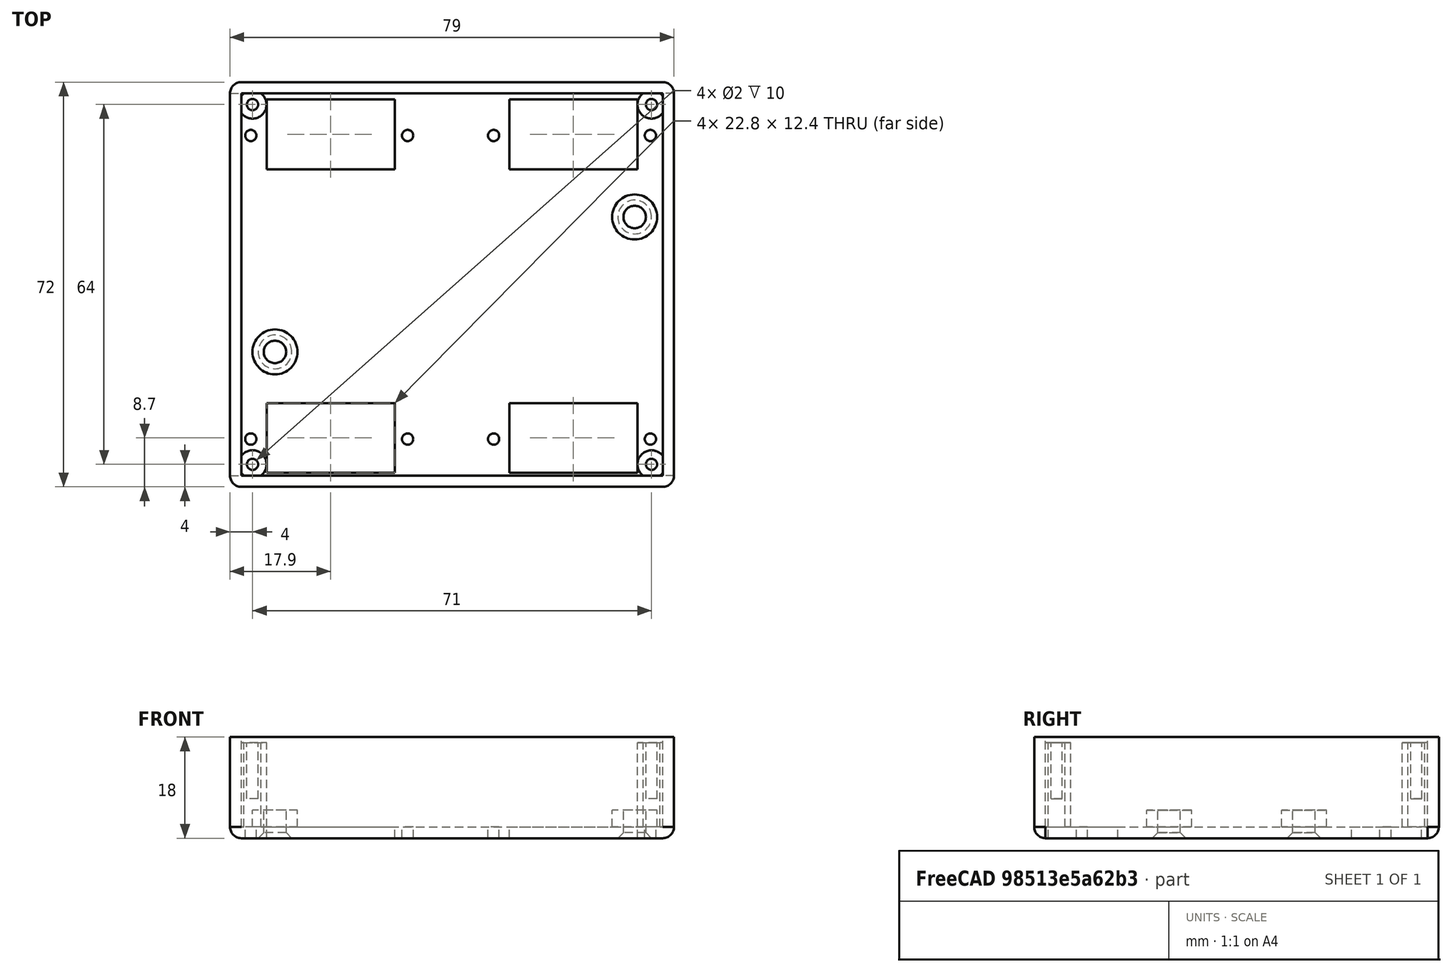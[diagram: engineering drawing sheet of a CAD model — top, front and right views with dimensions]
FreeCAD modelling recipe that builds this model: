
FCSTD DOCUMENT  (FreeCAD 0.18R16131 (Git))
Label: Level crossing base5 n gauge
License: All rights reserved
LicenseURL: http://en.wikipedia.org/wiki/All_rights_reserved
objects: PartDesign::LinearPattern×9, PartDesign::MultiTransform×4, PartDesign::SubtractiveCylinder×4, PartDesign::AdditiveCylinder×3, PartDesign::Chamfer×2, PartDesign::AdditiveBox×1, PartDesign::Thickness×1, PartDesign::SubtractiveBox×1, PartDesign::Body×1
note: 35 computed .brp shape members not serialized (recipe doc carries the construction recipe); baked Part::Feature solids carry a one-line shape summary decoded from their .brp

FEATURE [PartDesign::AdditiveBox] Box
  AttacherType = Attacher::AttachEngine3D
  Height = 16
  Length = 75
  MapMode = 5
  Support = -> [XY_Plane]
  Width = 67.45
FEATURE [PartDesign::Thickness] Thickness
  Base = -> Box [Face6]
  BaseFeature = -> Box
  Join = 0
  Mode = 0
  Value = 2
FEATURE [PartDesign::SubtractiveBox] Box001
  AttacherType = Attacher::AttachEngine3D
  AttachmentOffset = pos=(4.5,0.5,-2) rot=(0,0,1;0rad)
  BaseFeature = -> Thickness
  Height = 2
  Length = 22.8
  MapMode = 5
  Placement = pos=(4.5,0.5,-2) rot=(0,0,1;0rad)
  Support = -> [XY_Plane]
  Width = 12.4
FEATURE [PartDesign::LinearPattern] LinearPattern
  Direction = -> X_Axis
  Length = 43.2
  Occurrences = 2
  Placement = pos=(4.5,0.5,-2) rot=(0,0,1;0rad)
FEATURE [PartDesign::LinearPattern] LinearPattern001
  Direction = -> Y_Axis
  Length = 54
  Occurrences = 2
  Placement = pos=(4.5,0.5,-2) rot=(0,0,1;0rad)
FEATURE [PartDesign::MultiTransform] MultiTransform
  BaseFeature = -> Box001
  Originals = -> [Box001]
  Placement = pos=(4.5,0.5,-2) rot=(0,0,1;0rad)
  Transformations = -> [LinearPattern,LinearPattern001]
FEATURE [PartDesign::SubtractiveCylinder] Cylinder
  Angle = 360
  AttacherType = Attacher::AttachEngine3D
  AttachmentOffset = pos=(1.7,6.5,-2) rot=(0,0,1;0rad)
  BaseFeature = -> MultiTransform
  Height = 2
  MapMode = 5
  Placement = pos=(1.7,6.5,-2) rot=(0,0,1;0rad)
  Radius = 1
  Support = -> [XY_Plane]
FEATURE [PartDesign::LinearPattern] LinearPattern002
  Direction = -> X_Axis
  Length = 43.2
  Occurrences = 2
  Placement = pos=(1.7,6.5,-2) rot=(0,0,1;0rad)
FEATURE [PartDesign::LinearPattern] LinearPattern003
  Direction = -> Y_Axis
  Length = 54
  Occurrences = 2
  Placement = pos=(1.7,6.5,-2) rot=(0,0,1;0rad)
FEATURE [PartDesign::LinearPattern] LinearPattern004
  Direction = -> X_Axis
  Length = 27.9
  Occurrences = 2
  Placement = pos=(1.7,6.5,-2) rot=(0,0,1;0rad)
FEATURE [PartDesign::MultiTransform] MultiTransform001
  BaseFeature = -> Cylinder
  Originals = -> [Cylinder]
  Placement = pos=(1.7,6.5,-2) rot=(0,0,1;0rad)
  Transformations = -> [LinearPattern002,LinearPattern003,LinearPattern004]
FEATURE [PartDesign::AdditiveCylinder] Cylinder001
  Angle = 360
  AttacherType = Attacher::AttachEngine3D
  AttachmentOffset = pos=(2,2,0) rot=(0,0,1;0rad)
  BaseFeature = -> MultiTransform001
  Height = 15
  MapMode = 5
  Placement = pos=(2,2,0) rot=(0,0,1;0rad)
  Radius = 2.5
  Support = -> [XY_Plane]
FEATURE [PartDesign::LinearPattern] LinearPattern005
  Direction = -> X_Axis
  Length = 71
  Occurrences = 2
  Placement = pos=(2,2,0) rot=(0,0,1;0rad)
FEATURE [PartDesign::LinearPattern] LinearPattern006
  Direction = -> Y_Axis
  Length = 64
  Occurrences = 2
  Placement = pos=(2,2,0) rot=(0,0,1;0rad)
FEATURE [PartDesign::MultiTransform] MultiTransform002
  BaseFeature = -> Cylinder001
  Originals = -> [Cylinder001]
  Placement = pos=(2,2,0) rot=(0,0,1;0rad)
  Transformations = -> [LinearPattern005,LinearPattern006]
FEATURE [PartDesign::SubtractiveCylinder] Cylinder002
  Angle = 360
  AttacherType = Attacher::AttachEngine3D
  AttachmentOffset = pos=(0,0,-10) rot=(0,0,1;0rad)
  BaseFeature = -> MultiTransform002
  Height = 10
  MapMode = 5
  Placement = pos=(2,2,5) rot=(0,0,1;0rad)
  Radius = 1
  Support = -> [MultiTransform002]
FEATURE [PartDesign::LinearPattern] LinearPattern007
  Direction = -> X_Axis
  Length = 71
  Occurrences = 2
  Placement = pos=(2,2,5) rot=(0,0,1;0rad)
FEATURE [PartDesign::LinearPattern] LinearPattern008
  Direction = -> Y_Axis
  Length = 64
  Occurrences = 2
  Placement = pos=(2,2,5) rot=(0,0,1;0rad)
FEATURE [PartDesign::MultiTransform] MultiTransform003
  BaseFeature = -> Cylinder002
  Originals = -> [Cylinder002]
  Placement = pos=(2,2,5) rot=(0,0,1;0rad)
  Transformations = -> [LinearPattern007,LinearPattern008]
FEATURE [PartDesign::AdditiveCylinder] Cylinder003
  Angle = 360
  AttacherType = Attacher::AttachEngine3D
  AttachmentOffset = pos=(6,22,0) rot=(0,0,1;0rad)
  BaseFeature = -> MultiTransform003
  Height = 3
  MapMode = 5
  Placement = pos=(6,22,0) rot=(0,0,1;0rad)
  Radius = 4
  Support = -> [XY_Plane]
FEATURE [PartDesign::AdditiveCylinder] Cylinder004
  Angle = 360
  AttacherType = Attacher::AttachEngine3D
  AttachmentOffset = pos=(70,46,0) rot=(0,0,1;0rad)
  BaseFeature = -> Cylinder003
  Height = 3
  MapMode = 5
  Placement = pos=(70,46,0) rot=(0,0,1;0rad)
  Radius = 4
  Support = -> [XY_Plane]
FEATURE [PartDesign::SubtractiveCylinder] Cylinder005
  Angle = 360
  AttacherType = Attacher::AttachEngine3D
  AttachmentOffset = pos=(6,22,-2) rot=(0,0,1;0rad)
  BaseFeature = -> Cylinder004
  Height = 5
  MapMode = 5
  Placement = pos=(6,22,-2) rot=(0,0,1;0rad)
  Radius = 2
  Support = -> [XY_Plane]
FEATURE [PartDesign::SubtractiveCylinder] Cylinder006
  Angle = 360
  AttacherType = Attacher::AttachEngine3D
  AttachmentOffset = pos=(70,46,-2) rot=(0,0,1;0rad)
  BaseFeature = -> Cylinder005
  Height = 5
  MapMode = 5
  Placement = pos=(70,46,-2) rot=(0,0,1;0rad)
  Radius = 2
  Support = -> [XY_Plane]
FEATURE [PartDesign::Chamfer] Chamfer
  Base = -> Cylinder006 [Edge189]
  BaseFeature = -> Cylinder006
  Placement = pos=(70,46,-2) rot=(0,0,1;0rad)
  Size = 1
FEATURE [PartDesign::Chamfer] Chamfer001
  Base = -> Chamfer [Edge16]
  BaseFeature = -> Chamfer
  Placement = pos=(70,46,-2) rot=(0,0,1;0rad)
  Size = 1
FEATURE [PartDesign::Body] Body
  Group = -> [Box,Thickness,Box001,MultiTransform,LinearPattern,LinearPattern001,Cylinder,MultiTransform001,LinearPattern002,LinearPattern003,LinearPattern004,Cylinder001,MultiTransform002,LinearPattern005,LinearPattern006,Cylinder002,MultiTransform003,LinearPattern007,LinearPattern008,Cylinder003,Cylinder004,Cylinder005,Cylinder006,Chamfer,Chamfer001]
  Origin = -> Origin
  Tip = -> Chamfer001
